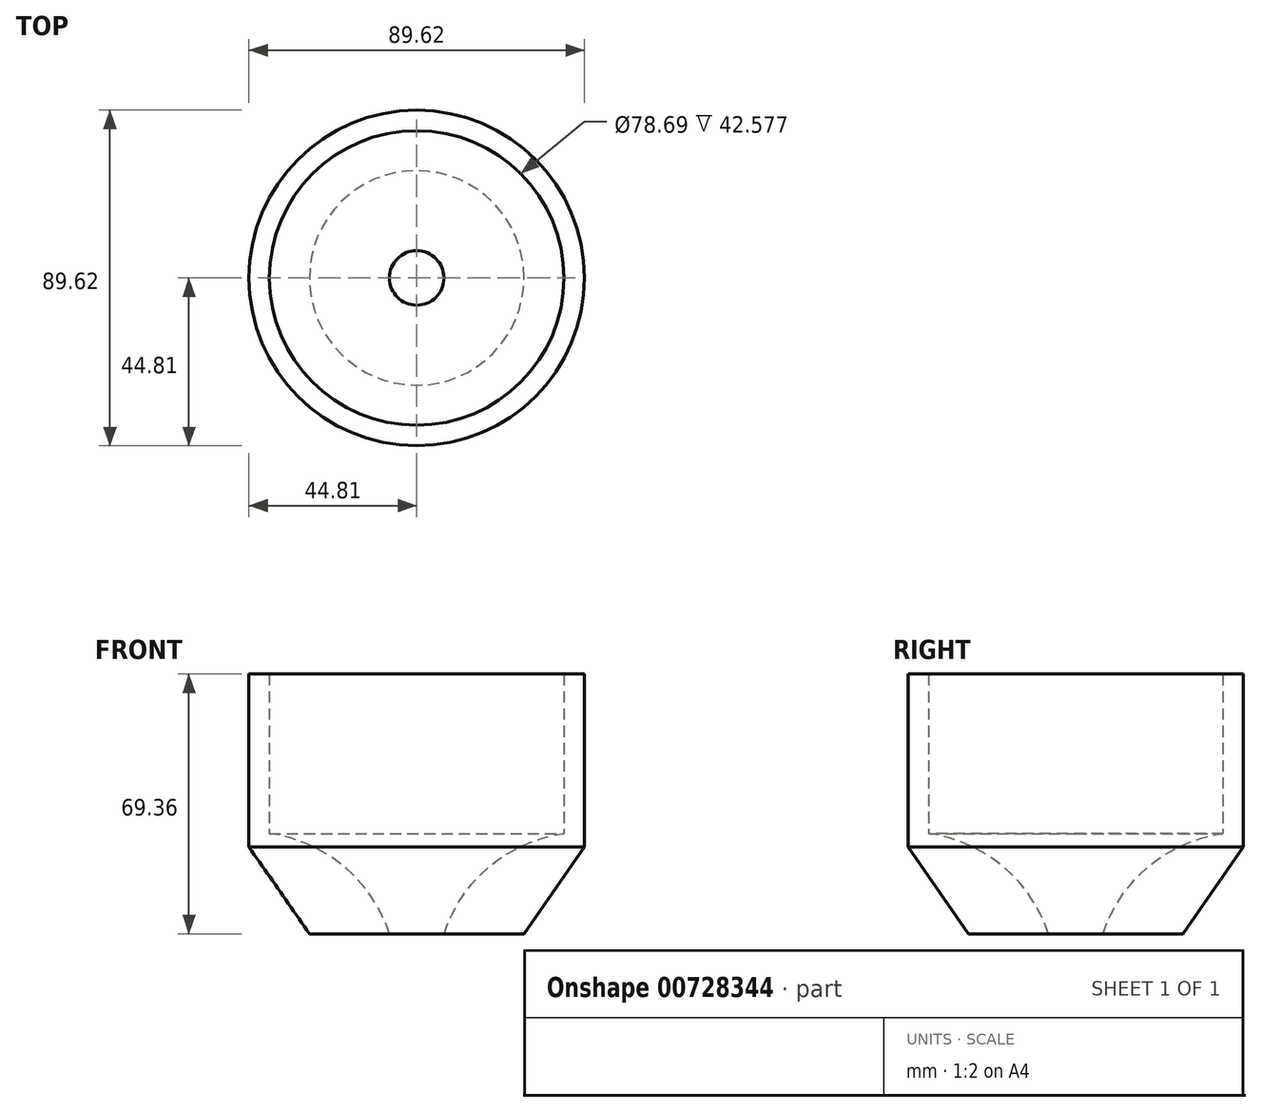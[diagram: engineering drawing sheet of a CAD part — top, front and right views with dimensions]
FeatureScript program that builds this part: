
annotation { "Feature Type Name" : "Feature", "Feature Type Description" : "" }
export const myFeature = defineFeature(function(context is Context, id is Id, definition is map)
    precondition{}
    {
        {
            var Q0;
            Q0=qCreatedBy(makeId("Right.planeOp"),FACE);
            var sketch = newSketch(context, id + "F0", { "sketchPlane" : qUnion([Q0])});
            skLineSegment(sketch, "E0", {"start": v(39.34, 26.79) * mm, "end": v(39.34, 69.36) * mm});
            skLineSegment(sketch, "E1", {"start": v(39.34, 69.36) * mm, "end": v(44.81, 69.36) * mm});
            skLineSegment(sketch, "E2", {"start": v(44.81, 69.36) * mm, "end": v(44.81, 23.2) * mm});
            skLineSegment(sketch, "E3", {"start": v(44.81, 23.2) * mm, "end": v(28.65, 0) * mm});
            skLineSegment(sketch, "E4", {"start": v(28.65, 0) * mm, "end": v(7.29, 0) * mm});
            skArc(sketch, "E5", {"start": v(39.34, 26.79) * mm, "mid": v(19.48, 17.98) * mm, "end": v(7.29, 0) * mm});
            skLineSegment(sketch, "E6", {"start": v(0, 0) * mm, "end": v(0, 71.48) * mm});
            skSolve(sketch);
        }
        {
            var Q0;
            Q0 = qSketchRegion(id + "F0", true);
            var Q1;
            Q1=sQuery(id+"F0.wireOp",EDGE,"E6");
            revolve(context, id + "F1", {"surfaceOperationType" : NewSurfaceOperationType.NEW, "entities" : qUnion([Q0]), "axis" : qUnion([Q1]), "revolveType" : RevolveType.FULL});
        }
    });
